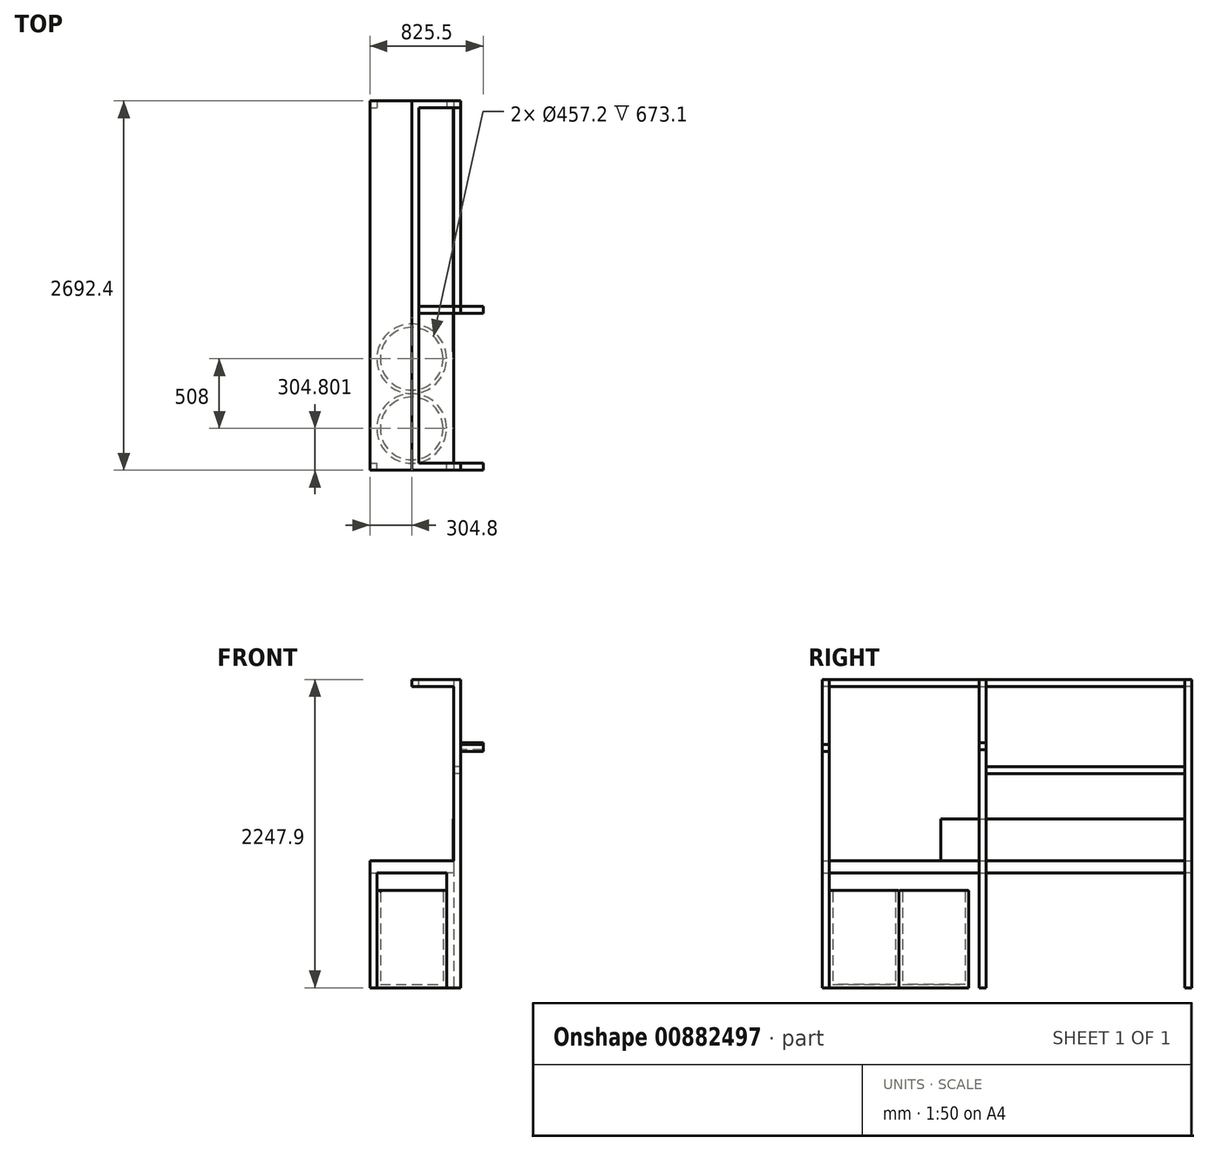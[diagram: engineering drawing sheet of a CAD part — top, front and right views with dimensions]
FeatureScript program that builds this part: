
annotation { "Feature Type Name" : "Feature", "Feature Type Description" : "" }
export const myFeature = defineFeature(function(context is Context, id is Id, definition is map)
    precondition{}
    {
        {
            var Q0;
            Q0=qCreatedBy(makeId("Right.planeOp"),FACE);
            var sketch = newSketch(context, id + "F0", { "sketchPlane" : qUnion([Q0])});
            skLineSegment(sketch, "E0.bottom", {"start": v(-1340.3, -28.95) * mm, "end": v(1352.1, -28.95) * mm});
            skLineSegment(sketch, "E0.top", {"start": v(-1340.3, -117.85) * mm, "end": v(1352.1, -117.85) * mm});
            skLineSegment(sketch, "E0.left", {"start": v(-1340.3, -28.95) * mm, "end": v(-1340.3, -117.85) * mm});
            skLineSegment(sketch, "E0.right", {"start": v(1352.1, -28.95) * mm, "end": v(1352.1, -117.85) * mm});
            skSolve(sketch);
        }
        {
            var Q0;
            Q0=makeQuery(id+"F0.imprint","IMPRINT",FACE,{"disambiguationData":[TD([[makeQuery(id+"F0.imprint","IMPRINT",EDGE,{"derivedFrom":sQuery(id+"F0.wireOp",EDGE,"E0.bottom")}),-1.0]])]});
            extrude(context, id + "F1", {"entities" : qUnion([Q0]), "oppositeDirection" : true, "depth" : 609.6 * mm, "offsetDistance" : 25.4 * mm});
        }
        {
            var Q0;
            Q0=makeQuery(id+"F1.opExtrude","SWEPT_FACE",FACE,{"disambiguationData":[OSD([sQuery(id+"F0.wireOp",EDGE,"E0.top")])]});
            var sketch = newSketch(context, id + "F2", { "sketchPlane" : qUnion([Q0])});
            skLineSegment(sketch, "E1.bottom", {"start": v(-609.6, 1340.3) * mm, "end": v(-558.8, 1340.3) * mm});
            skLineSegment(sketch, "E1.top", {"start": v(-609.6, 1289.5) * mm, "end": v(-558.8, 1289.5) * mm});
            skLineSegment(sketch, "E1.left", {"start": v(-609.6, 1340.3) * mm, "end": v(-609.6, 1289.5) * mm});
            skLineSegment(sketch, "E1.right", {"start": v(-558.8, 1340.3) * mm, "end": v(-558.8, 1289.5) * mm});
            skLineSegment(sketch, "E2.bottom", {"start": v(0, 1340.3) * mm, "end": v(-50.8, 1340.3) * mm});
            skLineSegment(sketch, "E2.top", {"start": v(0, 1289.5) * mm, "end": v(-50.8, 1289.5) * mm});
            skLineSegment(sketch, "E2.left", {"start": v(0, 1340.3) * mm, "end": v(0, 1289.5) * mm});
            skLineSegment(sketch, "E2.right", {"start": v(-50.8, 1340.3) * mm, "end": v(-50.8, 1289.5) * mm});
            skLineSegment(sketch, "E3.bottom", {"start": v(0, -1352.1) * mm, "end": v(-50.8, -1352.1) * mm});
            skLineSegment(sketch, "E3.top", {"start": v(0, -1301.3) * mm, "end": v(-50.8, -1301.3) * mm});
            skLineSegment(sketch, "E3.left", {"start": v(0, -1352.1) * mm, "end": v(0, -1301.3) * mm});
            skLineSegment(sketch, "E3.right", {"start": v(-50.8, -1352.1) * mm, "end": v(-50.8, -1301.3) * mm});
            skLineSegment(sketch, "E4.bottom", {"start": v(-609.6, -1352.1) * mm, "end": v(-558.8, -1352.1) * mm});
            skLineSegment(sketch, "E4.top", {"start": v(-609.6, -1301.3) * mm, "end": v(-558.8, -1301.3) * mm});
            skLineSegment(sketch, "E4.left", {"start": v(-609.6, -1352.1) * mm, "end": v(-609.6, -1301.3) * mm});
            skLineSegment(sketch, "E4.right", {"start": v(-558.8, -1352.1) * mm, "end": v(-558.8, -1301.3) * mm});
            skSolve(sketch);
        }
        {
            var Q0;
            Q0 = qSketchRegion(id + "F2", true);
            extrude(context, id + "F3", {"entities" : qUnion([Q0]), "operationType" : NewBodyOperationType.ADD, "depth" : 838.2 * mm, "offsetDistance" : 25.4 * mm});
        }
        {
            var Q0;
            Q0=makeQuery(id+"F3.opExtrude","CAP_FACE",FACE,{"disambiguationData":[OSD([sQuery(id+"F2.wireOp",EDGE,"E4.bottom"),sQuery(id+"F2.wireOp",EDGE,"E4.top"),sQuery(id+"F2.wireOp",EDGE,"E4.left"),sQuery(id+"F2.wireOp",EDGE,"E4.right")])],"isStart":false});
            var sketch = newSketch(context, id + "F4", { "sketchPlane" : qUnion([Q0])});
            skCircle(sketch, "E5", {"center": v(-304.8, 1035.5) * mm, "radius": 254 * mm});
            skCircle(sketch, "E6", {"center": v(-304.8, 527.5) * mm, "radius": 254 * mm});
            skSolve(sketch);
        }
        {
            var Q0;
            Q0 = qSketchRegion(id + "F4", true);
            extrude(context, id + "F5", {"entities" : qUnion([Q0]), "oppositeDirection" : true, "depth" : 711.2 * mm, "offsetDistance" : 25.4 * mm});
        }
        {
            var Q0;
            Q0=makeQuery(id+"F3.opExtrude","CAP_FACE",FACE,{"disambiguationData":[OSD([sQuery(id+"F2.wireOp",EDGE,"E2.bottom"),sQuery(id+"F2.wireOp",EDGE,"E2.top"),sQuery(id+"F2.wireOp",EDGE,"E2.left"),sQuery(id+"F2.wireOp",EDGE,"E2.right")])],"isStart":false});
            var sketch = newSketch(context, id + "F6", { "sketchPlane" : qUnion([Q0])});
            skLineSegment(sketch, "E7.bottom", {"start": v(0, 1340.3) * mm, "end": v(50.8, 1340.3) * mm});
            skLineSegment(sketch, "E7.top", {"start": v(0, 1289.5) * mm, "end": v(50.8, 1289.5) * mm});
            skLineSegment(sketch, "E7.left", {"start": v(0, 1340.3) * mm, "end": v(0, 1289.5) * mm});
            skLineSegment(sketch, "E7.right", {"start": v(50.8, 1340.3) * mm, "end": v(50.8, 1289.5) * mm});
            skLineSegment(sketch, "E8.bottom", {"start": v(0, -1301.3) * mm, "end": v(50.8, -1301.3) * mm});
            skLineSegment(sketch, "E8.top", {"start": v(0, -1352.1) * mm, "end": v(50.8, -1352.1) * mm});
            skLineSegment(sketch, "E8.left", {"start": v(0, -1301.3) * mm, "end": v(0, -1352.1) * mm});
            skLineSegment(sketch, "E8.right", {"start": v(50.8, -1301.3) * mm, "end": v(50.8, -1352.1) * mm});
            skSolve(sketch);
        }
        {
            var Q0;
            Q0 = qSketchRegion(id + "F6", true);
            extrude(context, id + "F7", {"entities" : qUnion([Q0]), "operationType" : NewBodyOperationType.ADD, "oppositeDirection" : true, "depth" : 2247.9 * mm, "offsetDistance" : 25.4 * mm});
        }
        {
            var Q0;
            Q0=makeQuery(id+"F7.opExtrude","SWEPT_FACE",FACE,{"disambiguationData":[OSD([sQuery(id+"F6.wireOp",EDGE,"E8.left")])]});
            var sketch = newSketch(context, id + "F8", { "sketchPlane" : qUnion([Q0])});
            skLineSegment(sketch, "E9.bottom", {"start": v(-1352.1, 1291.85) * mm, "end": v(1340.3, 1291.85) * mm});
            skLineSegment(sketch, "E9.top", {"start": v(-1352.1, 1241.05) * mm, "end": v(1340.3, 1241.05) * mm});
            skLineSegment(sketch, "E9.left", {"start": v(-1352.1, 1291.85) * mm, "end": v(-1352.1, 1241.05) * mm});
            skLineSegment(sketch, "E9.right", {"start": v(1340.3, 1291.85) * mm, "end": v(1340.3, 1241.05) * mm});
            skSolve(sketch);
        }
        {
            var Q0;
            Q0 = qSketchRegion(id + "F8", true);
            extrude(context, id + "F9", {"entities" : qUnion([Q0]), "operationType" : NewBodyOperationType.ADD, "depth" : 304.8 * mm, "offsetDistance" : 25.4 * mm});
        }
        {
            var Q0;
            Q0=makeQuery(id+"F9.boolean.opBoolean","MERGE",FACE,{"derivedFrom":[makeQuery(id+"F7.opExtrude","CAP_FACE",FACE,{"disambiguationData":[OSD([sQuery(id+"F6.wireOp",EDGE,"E7.bottom"),sQuery(id+"F6.wireOp",EDGE,"E7.top"),sQuery(id+"F6.wireOp",EDGE,"E7.left"),sQuery(id+"F6.wireOp",EDGE,"E7.right")])],"isStart":false}),makeQuery(id+"F7.opExtrude","CAP_FACE",FACE,{"disambiguationData":[OSD([sQuery(id+"F6.wireOp",EDGE,"E8.bottom"),sQuery(id+"F6.wireOp",EDGE,"E8.top"),sQuery(id+"F6.wireOp",EDGE,"E8.left"),sQuery(id+"F6.wireOp",EDGE,"E8.right")])],"isStart":false}),makeQuery(id+"F9.opExtrude","SWEPT_FACE",FACE,{"disambiguationData":[OSD([sQuery(id+"F8.wireOp",EDGE,"E9.bottom")])]})]});
            var sketch = newSketch(context, id + "F10", { "sketchPlane" : qUnion([Q0])});
            skLineSegment(sketch, "E10.bottom", {"start": v(0, 1301.3) * mm, "end": v(-254, 1301.3) * mm});
            skLineSegment(sketch, "E10.top", {"start": v(0, -1289.5) * mm, "end": v(-254, -1289.5) * mm});
            skLineSegment(sketch, "E10.left", {"start": v(0, 1301.3) * mm, "end": v(0, -1289.5) * mm});
            skLineSegment(sketch, "E10.right", {"start": v(-254, 1301.3) * mm, "end": v(-254, -1289.5) * mm});
            skSolve(sketch);
        }
        {
            var Q0;
            Q0 = qSketchRegion(id + "F10", true);
            extrude(context, id + "F11", {"entities" : qUnion([Q0]), "operationType" : NewBodyOperationType.REMOVE, "endBound" : BoundingType.UP_TO_NEXT, "oppositeDirection" : true, "depth" : 25.4 * mm, "offsetDistance" : 25.4 * mm});
        }
        {
            var Q0;
            Q0=makeQuery(id+"F1.opExtrude","SWEPT_FACE",FACE,{"disambiguationData":[OSD([sQuery(id+"F0.wireOp",EDGE,"E0.bottom")])]});
            var sketch = newSketch(context, id + "F12", { "sketchPlane" : qUnion([Q0])});
            skLineSegment(sketch, "E11.bottom", {"start": v(0, 1301.3) * mm, "end": v(-3.17, 1301.3) * mm});
            skLineSegment(sketch, "E11.top", {"start": v(0, -476.7) * mm, "end": v(-3.17, -476.7) * mm});
            skLineSegment(sketch, "E11.left", {"start": v(0, 1301.3) * mm, "end": v(0, -476.7) * mm});
            skLineSegment(sketch, "E11.right", {"start": v(-3.17, 1301.3) * mm, "end": v(-3.17, -476.7) * mm});
            skSolve(sketch);
        }
        {
            var Q0;
            Q0 = qSketchRegion(id + "F12", true);
            extrude(context, id + "F13", {"entities" : qUnion([Q0]), "depth" : 304.8 * mm, "offsetDistance" : 25.4 * mm});
        }
        {
            var Q0;
            Q0=makeQuery(id+"F7.boolean.opBoolean","MERGE",FACE,{"derivedFrom":[makeQuery(id+"F3.opExtrude","CAP_FACE",FACE,{"disambiguationData":[OSD([sQuery(id+"F2.wireOp",EDGE,"E2.bottom"),sQuery(id+"F2.wireOp",EDGE,"E2.top"),sQuery(id+"F2.wireOp",EDGE,"E2.left"),sQuery(id+"F2.wireOp",EDGE,"E2.right")])],"isStart":false}),makeQuery(id+"F7.opExtrude","CAP_FACE",FACE,{"disambiguationData":[OSD([sQuery(id+"F6.wireOp",EDGE,"E7.bottom"),sQuery(id+"F6.wireOp",EDGE,"E7.top"),sQuery(id+"F6.wireOp",EDGE,"E7.left"),sQuery(id+"F6.wireOp",EDGE,"E7.right")])],"isStart":true})]});
            var sketch = newSketch(context, id + "F14", { "sketchPlane" : qUnion([Q0])});
            skLineSegment(sketch, "E12.bottom", {"start": v(0, 197.3) * mm, "end": v(50.8, 197.3) * mm});
            skLineSegment(sketch, "E12.top", {"start": v(0, 146.5) * mm, "end": v(50.8, 146.5) * mm});
            skLineSegment(sketch, "E12.left", {"start": v(0, 197.3) * mm, "end": v(0, 146.5) * mm});
            skLineSegment(sketch, "E12.right", {"start": v(50.8, 197.3) * mm, "end": v(50.8, 146.5) * mm});
            skSolve(sketch);
        }
        {
            var Q0;
            Q0 = qSketchRegion(id + "F14", true);
            extrude(context, id + "F15", {"entities" : qUnion([Q0]), "oppositeDirection" : true, "depth" : 2247.9 * mm, "offsetDistance" : 25.4 * mm});
        }
        {
            var Q0;
            Q0=makeQuery(id+"F5.opExtrude","CAP_FACE",FACE,{"disambiguationData":[OSD([sQuery(id+"F4.wireOp",EDGE,"E6")])],"isStart":false});
            shell(context, id + "F16", {"entities" : qUnion([Q0]), "thickness" : 25.4 * mm});
        }
        {
            var Q0;
            Q0=makeQuery(id+"F5.opExtrude","CAP_FACE",FACE,{"disambiguationData":[OSD([sQuery(id+"F4.wireOp",EDGE,"E5")])],"isStart":false});
            shell(context, id + "F17", {"entities" : qUnion([Q0]), "thickness" : 25.4 * mm});
        }
        {
            var Q0;
            Q0=makeQuery(id+"F5.opExtrude","CAP_FACE",FACE,{"disambiguationData":[OSD([sQuery(id+"F4.wireOp",EDGE,"E5")])],"isStart":false});
            fillet(context, id + "F18", {"entities" : qUnion([Q0]), "radius" : 12.7 * mm, "tangentPropagation" : true, "allowEdgeOverflow" : false});
        }
        {
            var Q0;
            Q0=makeQuery(id+"F5.opExtrude","CAP_FACE",FACE,{"disambiguationData":[OSD([sQuery(id+"F4.wireOp",EDGE,"E6")])],"isStart":false});
            fillet(context, id + "F19", {"entities" : qUnion([Q0]), "radius" : 12.7 * mm, "tangentPropagation" : true, "allowEdgeOverflow" : false});
        }
        {
            var Q0;
            Q0=makeQuery(id+"F11.boolean.opBoolean","MERGE",FACE,{"derivedFrom":[makeQuery(id+"F7.boolean.opBoolean","MERGE",FACE,{"derivedFrom":[makeQuery(id+"F3.opExtrude","SWEPT_FACE",FACE,{"disambiguationData":[OSD([sQuery(id+"F2.wireOp",EDGE,"E3.top")])]}),makeQuery(id+"F7.opExtrude","SWEPT_FACE",FACE,{"disambiguationData":[OSD([sQuery(id+"F6.wireOp",EDGE,"E8.bottom")])]})]})],"fromTools":[makeQuery(id+"F11.opExtrude","SWEPT_FACE",FACE,{"disambiguationData":[OSD([sQuery(id+"F10.wireOp",EDGE,"E10.bottom")])]})]});
            var sketch = newSketch(context, id + "F20", { "sketchPlane" : qUnion([Q0])});
            skLineSegment(sketch, "E13.bottom", {"start": v(0, 656.85) * mm, "end": v(50.8, 656.85) * mm});
            skLineSegment(sketch, "E13.top", {"start": v(0, 606.05) * mm, "end": v(50.8, 606.05) * mm});
            skLineSegment(sketch, "E13.left", {"start": v(0, 656.85) * mm, "end": v(0, 606.05) * mm});
            skLineSegment(sketch, "E13.right", {"start": v(50.8, 656.85) * mm, "end": v(50.8, 606.05) * mm});
            skSolve(sketch);
        }
        {
            var Q0;
            Q0 = qSketchRegion(id + "F20", true);
            extrude(context, id + "F21", {"entities" : qUnion([Q0]), "endBound" : BoundingType.UP_TO_NEXT, "depth" : 25.4 * mm, "offsetDistance" : 25.4 * mm});
        }
        {
            var Q0;
            Q0=makeQuery(id+"F15.opExtrude","SWEPT_FACE",FACE,{"disambiguationData":[OSD([sQuery(id+"F14.wireOp",EDGE,"E12.right")])]});
            var sketch = newSketch(context, id + "F22", { "sketchPlane" : qUnion([Q0])});
            skLineSegment(sketch, "E14.bottom", {"start": v(-197.3, 831.1) * mm, "end": v(-146.5, 831.1) * mm});
            skLineSegment(sketch, "E14.top", {"start": v(-197.3, 780.3) * mm, "end": v(-146.5, 780.3) * mm});
            skLineSegment(sketch, "E14.left", {"start": v(-197.3, 831.1) * mm, "end": v(-197.3, 780.3) * mm});
            skLineSegment(sketch, "E14.right", {"start": v(-146.5, 831.1) * mm, "end": v(-146.5, 780.3) * mm});
            skLineSegment(sketch, "E15.bottom", {"start": v(-1340.3, 818.75) * mm, "end": v(-1289.5, 818.75) * mm});
            skLineSegment(sketch, "E15.top", {"start": v(-1340.3, 767.95) * mm, "end": v(-1289.5, 767.95) * mm});
            skLineSegment(sketch, "E15.left", {"start": v(-1340.3, 818.75) * mm, "end": v(-1340.3, 767.95) * mm});
            skLineSegment(sketch, "E15.right", {"start": v(-1289.5, 818.75) * mm, "end": v(-1289.5, 767.95) * mm});
            skSolve(sketch);
        }
        {
            var Q0;
            Q0 = qSketchRegion(id + "F22", true);
            extrude(context, id + "F23", {"entities" : qUnion([Q0]), "depth" : 165.1 * mm, "offsetDistance" : 25.4 * mm});
        }
        {
            var Q0;
            Q0=makeQuery(id+"F15.opExtrude","SWEPT_FACE",FACE,{"disambiguationData":[OSD([sQuery(id+"F14.wireOp",EDGE,"E12.left")])]});
            var sketch = newSketch(context, id + "F24", { "sketchPlane" : qUnion([Q0])});
            skLineSegment(sketch, "E16.bottom", {"start": v(146.5, 1291.85) * mm, "end": v(197.3, 1291.85) * mm});
            skLineSegment(sketch, "E16.top", {"start": v(146.5, 1241.05) * mm, "end": v(197.3, 1241.05) * mm});
            skLineSegment(sketch, "E16.left", {"start": v(146.5, 1291.85) * mm, "end": v(146.5, 1241.05) * mm});
            skLineSegment(sketch, "E16.right", {"start": v(197.3, 1291.85) * mm, "end": v(197.3, 1241.05) * mm});
            skSolve(sketch);
        }
        {
            var Q0;
            Q0 = qSketchRegion(id + "F24", true);
            extrude(context, id + "F25", {"entities" : qUnion([Q0]), "endBound" : BoundingType.UP_TO_NEXT, "depth" : 25.4 * mm, "offsetDistance" : 25.4 * mm});
        }
    });
